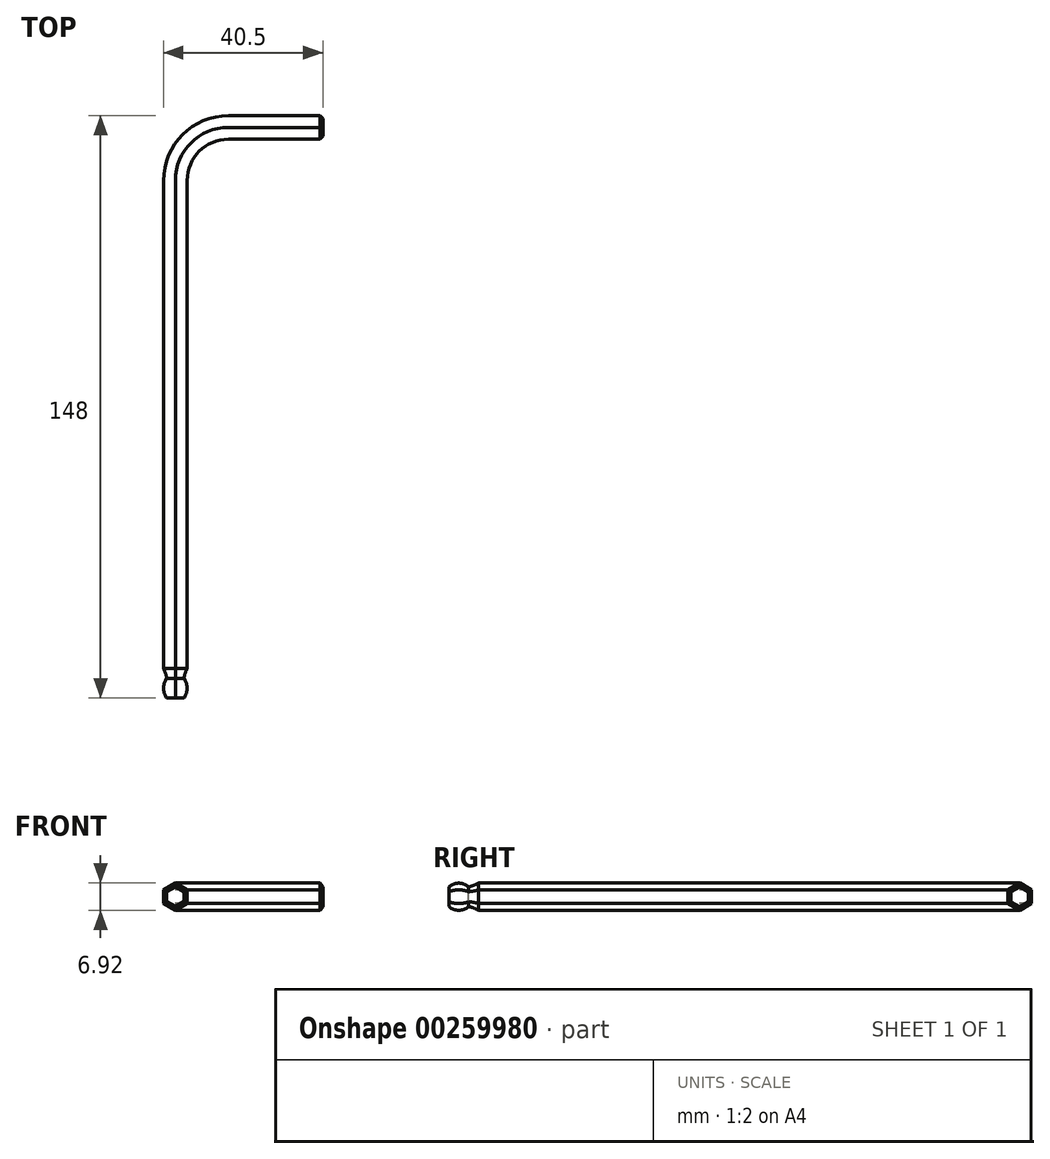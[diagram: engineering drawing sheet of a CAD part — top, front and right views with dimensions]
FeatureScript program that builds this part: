
annotation { "Feature Type Name" : "Feature", "Feature Type Description" : "" }
export const myFeature = defineFeature(function(context is Context, id is Id, definition is map)
    precondition{}
    {
        {
            var Q0;
            Q0=qCreatedBy(makeId("Top.planeOp"),FACE);
            var sketch = newSketch(context, id + "F0", { "sketchPlane" : qUnion([Q0]), "disableImprinting" : false});
            skLineSegment(sketch, "E0", {"start": v(0, 0) * mm, "end": v(0, 131.5) * mm});
            skArc(sketch, "E1", {"start": v(13.5, 145) * mm, "mid": v(3.95, 141.05) * mm, "end": v(0, 131.5) * mm});
            skLineSegment(sketch, "E2", {"start": v(13.5, 145) * mm, "end": v(37.5, 145) * mm});
            skSolve(sketch);
        }
        {
            var Q0;
            Q0=qCreatedBy(makeId("Right.planeOp"),FACE);
            cPlane(context, id + "F1", {"entities" : qUnion([Q0]), "cplaneType" : CPlaneType.OFFSET, "offset" : 37.5 * mm, "width" : 150 * mm, "height" : 150 * mm});
        }
        {
            var Q0;
            Q0=qCreatedBy(id+"F1.planeOp",FACE);
            var sketch = newSketch(context, id + "F2", { "sketchPlane" : qUnion([Q0])});
            skCircle(sketch, "E3.cCircle", {"center": v(145, 0) * mm, "radius": 3 * mm, "construction": true});
            skLineSegment(sketch, "E3.0", {"start": v(142, -1.73) * mm, "end": v(142, 1.73) * mm});
            skLineSegment(sketch, "E3.1", {"start": v(142, 1.73) * mm, "end": v(145, 3.46) * mm});
            skLineSegment(sketch, "E3.2", {"start": v(145, 3.46) * mm, "end": v(148, 1.73) * mm});
            skLineSegment(sketch, "E3.3", {"start": v(148, 1.73) * mm, "end": v(148, -1.73) * mm});
            skLineSegment(sketch, "E3.4", {"start": v(148, -1.73) * mm, "end": v(145, -3.46) * mm});
            skLineSegment(sketch, "E3.5", {"start": v(145, -3.46) * mm, "end": v(142, -1.73) * mm});
            skPoint(sketch, "E3.0.midPoint", {"position": v(142, 0) * mm});
            skSolve(sketch);
        }
        {
            var Q0;
            Q0=makeQuery(id+"F2.imprint","IMPRINT",FACE,{"disambiguationData":[TD([[makeQuery(id+"F2.imprint","IMPRINT",EDGE,{"derivedFrom":sQuery(id+"F2.wireOp",EDGE,"E3.0")}),-1.0]])]});
            var Q1;
            Q1=qConstructionFilter(qBodyType(qCreatedBy(id+"F0",EDGE),BodyType.WIRE),ConstructionObject.NO);
            sweep(context, id + "F3", {"profiles" : qUnion([Q0]), "path" : qUnion([Q1])});
        }
        {
            var Q0;
            Q0=makeQuery(id+"F3.opSweep","CAP_FACE",FACE,{"disambiguationData":[OSD([sQuery(id+"F0.wireOp",VERTEX,"E2.end"),sQuery(id+"F2.wireOp",EDGE,"E3.0"),sQuery(id+"F2.wireOp",EDGE,"E3.1"),sQuery(id+"F2.wireOp",EDGE,"E3.2"),sQuery(id+"F2.wireOp",EDGE,"E3.3"),sQuery(id+"F2.wireOp",EDGE,"E3.4"),sQuery(id+"F2.wireOp",EDGE,"E3.5")])],"isStart":true});
            chamfer(context, id + "F4", {"entities" : qUnion([Q0]), "width" : .8 * mm, "tangentPropagation" : true});
        }
        {
            var Q0;
            Q0=qCreatedBy(makeId("Right.planeOp"),FACE);
            var sketch = newSketch(context, id + "F5", { "sketchPlane" : qUnion([Q0])});
            skArc(sketch, "E4", {"start": v(7.5, -3.46) * mm, "mid": v(6.29, -2.88) * mm, "end": v(5, -2.5) * mm});
            skArc(sketch, "E5", {"start": v(0, -2.5) * mm, "mid": v(2.5, -3.45) * mm, "end": v(5, -2.5) * mm});
            skLineSegment(sketch, "E6", {"start": v(7.5, -3.46) * mm, "end": v(7.5, -5.5) * mm});
            skLineSegment(sketch, "E7", {"start": v(7.5, -5.5) * mm, "end": v(0, -5.5) * mm});
            skLineSegment(sketch, "E8", {"start": v(0, -5.5) * mm, "end": v(0, -2.5) * mm});
            skSolve(sketch);
        }
        {
            var Q0;
            Q0=qSketchRegion(id+"F5",true);
            var Q1;
            Q1=makeQuery(id+"F3.opSweep","CAP_EDGE",EDGE,{"disambiguationData":[OSD([sQuery(id+"F0.wireOp",VERTEX,"E0.start"),sQuery(id+"F2.wireOp",EDGE,"E3.4")])],"isStart":false});
            var Q2;
            Q2=makeQuery(id+"F3.opSweep","CAP_EDGE",EDGE,{"disambiguationData":[OSD([sQuery(id+"F0.wireOp",VERTEX,"E0.start"),sQuery(id+"F2.wireOp",EDGE,"E3.3")])],"isStart":false});
            var Q3;
            Q3=makeQuery(id+"F3.opSweep","CAP_EDGE",EDGE,{"disambiguationData":[OSD([sQuery(id+"F0.wireOp",VERTEX,"E0.start"),sQuery(id+"F2.wireOp",EDGE,"E3.2")])],"isStart":false});
            var Q4;
            Q4=makeQuery(id+"F3.opSweep","CAP_EDGE",EDGE,{"disambiguationData":[OSD([sQuery(id+"F0.wireOp",VERTEX,"E0.start"),sQuery(id+"F2.wireOp",EDGE,"E3.1")])],"isStart":false});
            var Q5;
            Q5=makeQuery(id+"F3.opSweep","CAP_EDGE",EDGE,{"disambiguationData":[OSD([sQuery(id+"F0.wireOp",VERTEX,"E0.start"),sQuery(id+"F2.wireOp",EDGE,"E3.0")])],"isStart":false});
            var Q6;
            Q6=makeQuery(id+"F3.opSweep","CAP_EDGE",EDGE,{"disambiguationData":[OSD([sQuery(id+"F0.wireOp",VERTEX,"E0.start"),sQuery(id+"F2.wireOp",EDGE,"E3.5")])],"isStart":false});
            sweep(context, id + "F6", {"operationType" : NewBodyOperationType.REMOVE, "profiles" : qUnion([Q0]), "path" : qUnion([Q1, Q2, Q3, Q4, Q5, Q6])});
        }
    });
